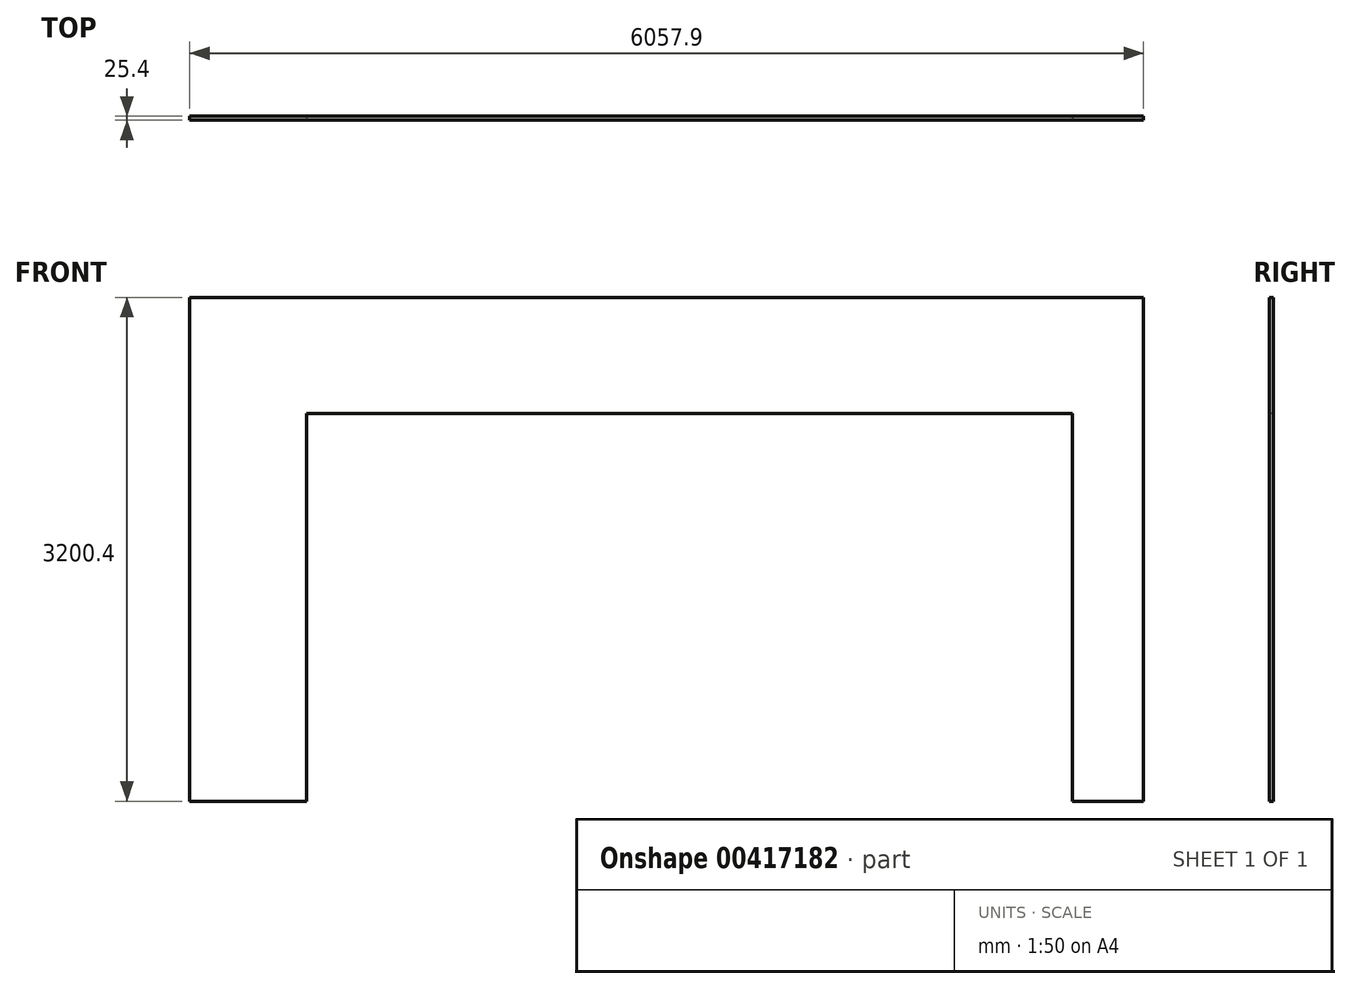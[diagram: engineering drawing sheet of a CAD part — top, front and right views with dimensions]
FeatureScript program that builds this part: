
annotation { "Feature Type Name" : "Feature", "Feature Type Description" : "" }
export const myFeature = defineFeature(function(context is Context, id is Id, definition is map)
    precondition{}
    {
        {
            var Q0;
            Q0=qCreatedBy(makeId("Front.planeOp"),FACE);
            var sketch = newSketch(context, id + "F0", { "sketchPlane" : qUnion([Q0])});
            skLineSegment(sketch, "E0.bottom", {"start": v(0, 0) * mm, "end": v(742.95, 0) * mm});
            skLineSegment(sketch, "E0.top", {"start": v(0, 3200.4) * mm, "end": v(6057.9, 3200.4) * mm});
            skLineSegment(sketch, "E0.left", {"start": v(0, 0) * mm, "end": v(0, 3200.4) * mm});
            skLineSegment(sketch, "E0.right", {"start": v(6057.9, 0) * mm, "end": v(6057.9, 3200.4) * mm});
            skLineSegment(sketch, "E1.top", {"start": v(742.95, 2463.8) * mm, "end": v(5607.05, 2463.8) * mm});
            skLineSegment(sketch, "E1.left", {"start": v(742.95, 0) * mm, "end": v(742.95, 2463.8) * mm});
            skLineSegment(sketch, "E1.right", {"start": v(5607.05, 0) * mm, "end": v(5607.05, 2463.8) * mm});
            skLineSegment(sketch, "E2.trimOffspring", {"start": v(5607.05, 0) * mm, "end": v(6057.9, 0) * mm});
            skSolve(sketch);
        }
        {
            var Q0;
            Q0=makeQuery(id+"F0.imprint","IMPRINT",FACE,{"disambiguationData":[TD([[makeQuery(id+"F0.imprint","IMPRINT",EDGE,{"derivedFrom":sQuery(id+"F0.wireOp",EDGE,"E0.bottom")}),1.0]])]});
            extrude(context, id + "F1", {"entities" : qUnion([Q0]), "oppositeDirection" : true, "depth" : 25.4 * mm});
        }
    });
